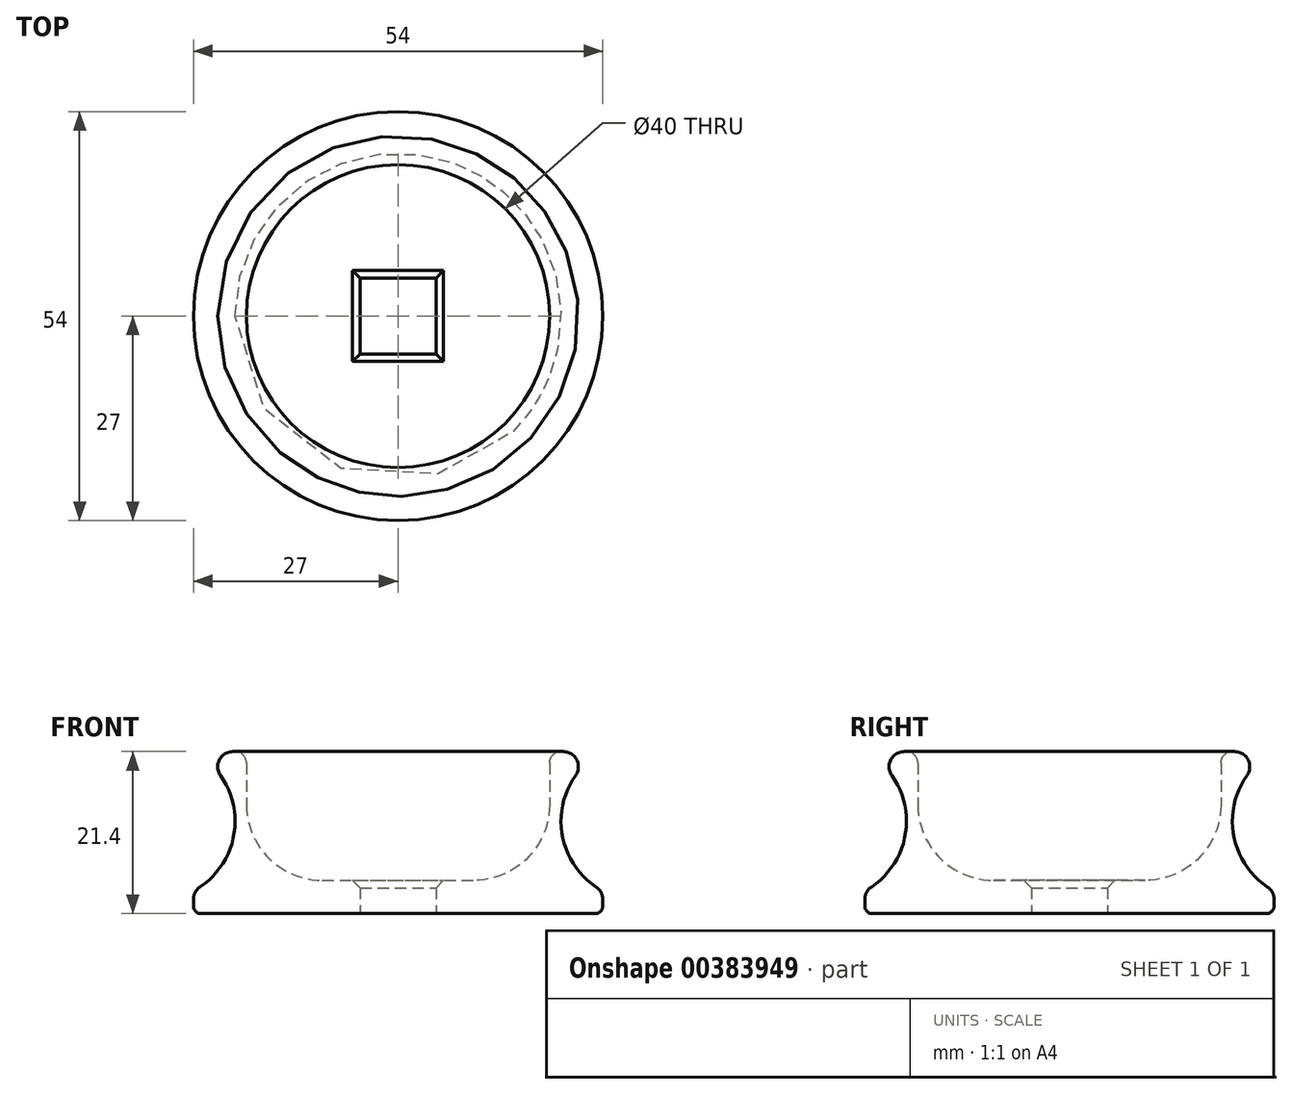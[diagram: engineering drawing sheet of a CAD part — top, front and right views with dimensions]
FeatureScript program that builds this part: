
annotation { "Feature Type Name" : "Feature", "Feature Type Description" : "" }
export const myFeature = defineFeature(function(context is Context, id is Id, definition is map)
    precondition{}
    {
        {
            var Q0;
            Q0=qCreatedBy(makeId("Front.planeOp"),FACE);
            var sketch = newSketch(context, id + "F0", { "sketchPlane" : qUnion([Q0])});
            skArc(sketch, "E0", {"start": v(-27, 0) * mm, "mid": v(-21.5, 9.2) * mm, "end": v(-27, 18.4) * mm});
            skLineSegment(sketch, "E1", {"start": v(0, 0) * mm, "end": v(0, 1.4) * mm});
            skLineSegment(sketch, "E2", {"start": v(0, 1.4) * mm, "end": v(-20, 1.4) * mm});
            skLineSegment(sketch, "E3", {"start": v(-20, 1.4) * mm, "end": v(-20, 18.4) * mm});
            skLineSegment(sketch, "E4", {"start": v(-20, 18.4) * mm, "end": v(-27, 18.4) * mm});
            skLineSegment(sketch, "E5", {"start": v(-27, 0) * mm, "end": v(-27, -3) * mm});
            skLineSegment(sketch, "E6", {"start": v(-27, -3) * mm, "end": v(0, -3) * mm});
            skLineSegment(sketch, "E7", {"start": v(0, -3) * mm, "end": v(0, 0) * mm});
            skSolve(sketch);
        }
        {
            var Q0;
            Q0=makeQuery(id+"F0.imprint","IMPRINT",FACE,{"disambiguationData":[TD([[makeQuery(id+"F0.imprint","IMPRINT",EDGE,{"derivedFrom":sQuery(id+"F0.wireOp",EDGE,"E0")}),-1.0]])]});
            var Q1;
            Q1=sQuery(id+"F0.wireOp",EDGE,"E1");
            revolve(context, id + "F1", {"entities" : qUnion([Q0]), "axis" : qUnion([Q1]), "revolveType" : RevolveType.FULL});
        }
        {
            var Q0;
            Q0=makeQuery(id+"F1.opRevolve","SWEPT_EDGE",EDGE,{"disambiguationData":[OSD([sQuery(id+"F0.wireOp",EDGE,"E2"),sQuery(id+"F0.wireOp",EDGE,"E3")])]});
            fillet(context, id + "F2", {"entities" : qUnion([Q0]), "radius" : 10 * mm, "tangentPropagation" : true, "allowEdgeOverflow" : false});
        }
        {
            var Q0;
            Q0=makeQuery(id+"F1.opRevolve","SWEPT_EDGE",EDGE,{"disambiguationData":[OSD([sQuery(id+"F0.wireOp",EDGE,"E0"),sQuery(id+"F0.wireOp",EDGE,"Yf9D9yeG-xyML-pteR-RfYU-DmGQTFrGGtZS")])]});
            fillet(context, id + "F3", {"entities" : qUnion([Q0]), "radius" : 2 * mm, "tangentPropagation" : true, "allowEdgeOverflow" : false});
        }
        {
            var Q0;
            Q0=makeQuery(id+"F1.opRevolve","SWEPT_EDGE",EDGE,{"disambiguationData":[OSD([sQuery(id+"F0.wireOp",EDGE,"E0"),sQuery(id+"F0.wireOp",EDGE,"E4")])]});
            var Q1;
            Q1=makeQuery(id+"F1.opRevolve","SWEPT_EDGE",EDGE,{"disambiguationData":[OSD([sQuery(id+"F0.wireOp",EDGE,"E3"),sQuery(id+"F0.wireOp",EDGE,"E4")])]});
            fillet(context, id + "F4", {"entities" : qUnion([Q0, Q1]), "radius" : 1.5 * mm, "tangentPropagation" : true, "allowEdgeOverflow" : false});
        }
        {
            var Q0;
            Q0=makeQuery(id+"F1.opRevolve","SWEPT_FACE",FACE,{"disambiguationData":[OSD([sQuery(id+"F0.wireOp",EDGE,"E6")])]});
            var sketch = newSketch(context, id + "F5", { "sketchPlane" : qUnion([Q0])});
            skLineSegment(sketch, "E8.bottom", {"start": v(5, 5) * mm, "end": v(-5, 5) * mm});
            skLineSegment(sketch, "E8.top", {"start": v(5, -5) * mm, "end": v(-5, -5) * mm});
            skLineSegment(sketch, "E8.left", {"start": v(5, 5) * mm, "end": v(5, -5) * mm});
            skLineSegment(sketch, "E8.right", {"start": v(-5, 5) * mm, "end": v(-5, -5) * mm});
            skPoint(sketch, "E8.middle", {"position": v(0, 0) * mm});
            skSolve(sketch);
        }
        {
            var Q0;
            Q0=makeQuery(id+"F5.imprint","IMPRINT",FACE,{"disambiguationData":[TD([[makeQuery(id+"F5.imprint","IMPRINT",EDGE,{"derivedFrom":sQuery(id+"F5.wireOp",EDGE,"E8.bottom")}),1.0]])]});
            extrude(context, id + "F6", {"entities" : qUnion([Q0]), "operationType" : NewBodyOperationType.REMOVE, "endBound" : BoundingType.THROUGH_ALL, "oppositeDirection" : true, "depth" : 1 * mm});
        }
        {
            var Q0;
            Q0=makeQuery(id+"F1.opRevolve","SWEPT_EDGE",EDGE,{"disambiguationData":[OSD([sQuery(id+"F0.wireOp",EDGE,"E5"),sQuery(id+"F0.wireOp",EDGE,"E6")])]});
            fillet(context, id + "F7", {"entities" : qUnion([Q0]), "radius" : 1 * mm, "allowEdgeOverflow" : false});
        }
        {
            var Q0;
            Q0=makeQuery(id+"F6.boolean.opBoolean","INTERSECT",EDGE,{"derivedFrom":[makeQuery(id+"F1.opRevolve","SWEPT_FACE",FACE,{"disambiguationData":[OSD([sQuery(id+"F0.wireOp",EDGE,"E2")])]}),makeQuery(id+"F6.opExtrude","SWEPT_FACE",FACE,{"disambiguationData":[OSD([sQuery(id+"F5.wireOp",EDGE,"E8.left")])]})]});
            var Q1;
            Q1=makeQuery(id+"F6.boolean.opBoolean","INTERSECT",EDGE,{"derivedFrom":[makeQuery(id+"F1.opRevolve","SWEPT_FACE",FACE,{"disambiguationData":[OSD([sQuery(id+"F0.wireOp",EDGE,"E2")])]}),makeQuery(id+"F6.opExtrude","SWEPT_FACE",FACE,{"disambiguationData":[OSD([sQuery(id+"F5.wireOp",EDGE,"E8.top")])]})]});
            var Q2;
            Q2=makeQuery(id+"F6.boolean.opBoolean","INTERSECT",EDGE,{"derivedFrom":[makeQuery(id+"F1.opRevolve","SWEPT_FACE",FACE,{"disambiguationData":[OSD([sQuery(id+"F0.wireOp",EDGE,"E2")])]}),makeQuery(id+"F6.opExtrude","SWEPT_FACE",FACE,{"disambiguationData":[OSD([sQuery(id+"F5.wireOp",EDGE,"E8.right")])]})]});
            var Q3;
            Q3=makeQuery(id+"F6.boolean.opBoolean","INTERSECT",EDGE,{"derivedFrom":[makeQuery(id+"F1.opRevolve","SWEPT_FACE",FACE,{"disambiguationData":[OSD([sQuery(id+"F0.wireOp",EDGE,"E2")])]}),makeQuery(id+"F6.opExtrude","SWEPT_FACE",FACE,{"disambiguationData":[OSD([sQuery(id+"F5.wireOp",EDGE,"E8.bottom")])]})]});
            chamfer(context, id + "F8", {"entities" : qUnion([Q0, Q1, Q2, Q3]), "width" : 1 * mm, "tangentPropagation" : true});
        }
    });
